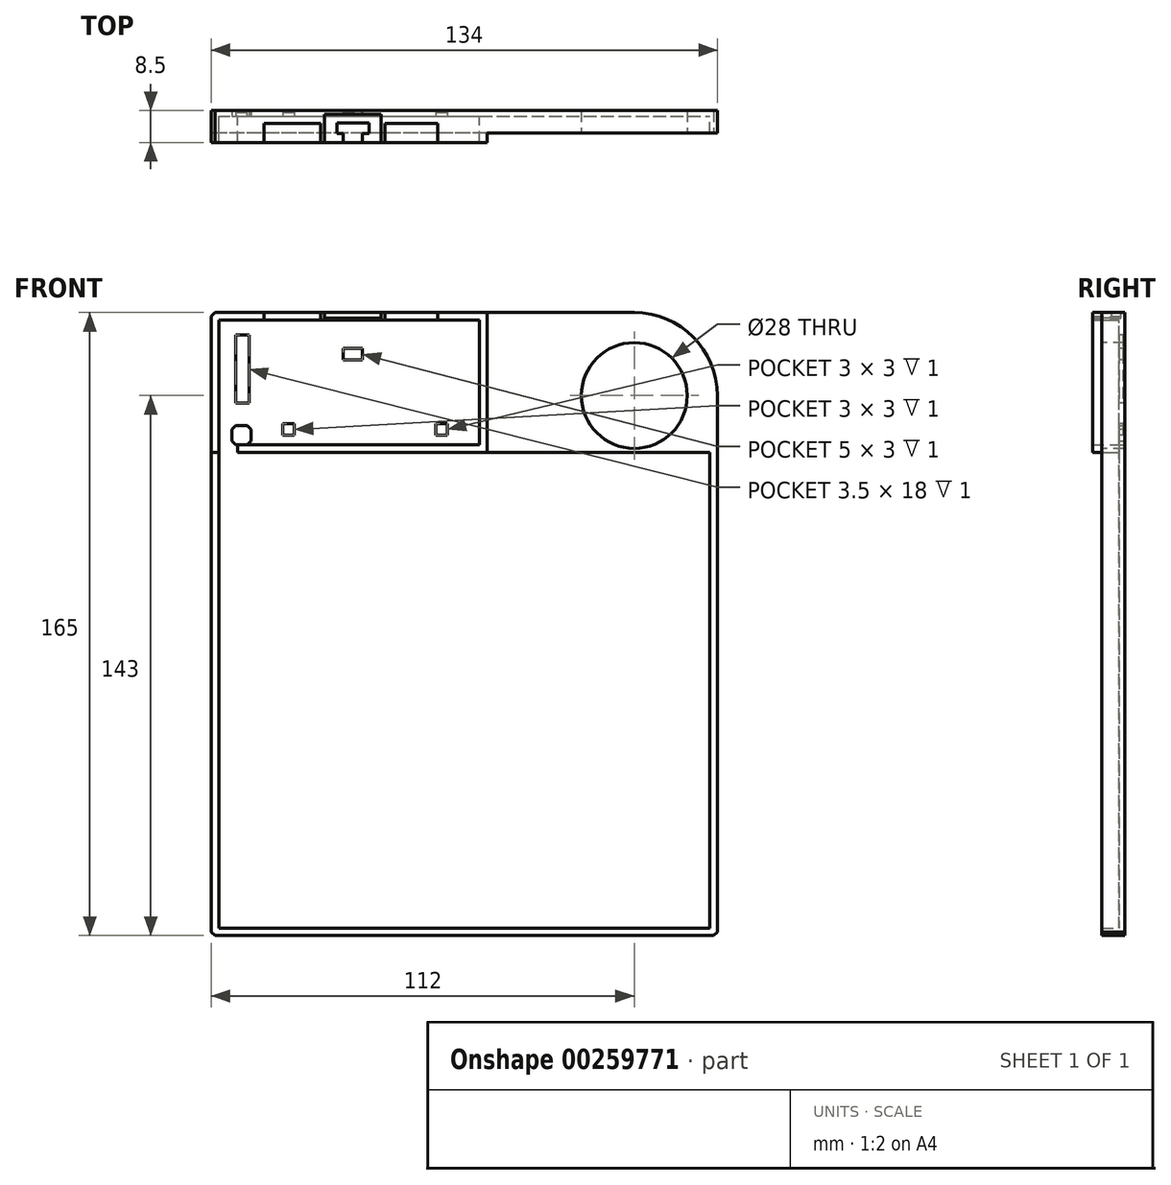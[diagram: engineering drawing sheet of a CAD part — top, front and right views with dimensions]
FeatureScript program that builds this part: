
annotation { "Feature Type Name" : "Feature", "Feature Type Description" : "" }
export const myFeature = defineFeature(function(context is Context, id is Id, definition is map)
    precondition{}
    {
        {
            var Q0;
            Q0=qCreatedBy(makeId("Front.planeOp"),FACE);
            var sketch = newSketch(context, id + "F0", { "sketchPlane" : qUnion([Q0])});
            skLineSegment(sketch, "E0.bottom", {"start": v(65, -63) * mm, "end": v(-65, -63) * mm});
            skLineSegment(sketch, "E0.top", {"start": v(65, 63) * mm, "end": v(-60, 63) * mm});
            skLineSegment(sketch, "E0.left", {"start": v(65, -63) * mm, "end": v(65, 63) * mm});
            skLineSegment(sketch, "E0.right", {"start": v(-65, -63) * mm, "end": v(-65, 63) * mm});
            skPoint(sketch, "E0.middle", {"position": v(0, 0) * mm});
            skLineSegment(sketch, "E1.0", {"start": v(67, -65) * mm, "end": v(-67, -65) * mm});
            skLineSegment(sketch, "E1.1", {"start": v(67, -65) * mm, "end": v(67, 65) * mm});
            skLineSegment(sketch, "E1.2", {"start": v(4, 65) * mm, "end": v(-60, 65) * mm});
            skLineSegment(sketch, "E1.3", {"start": v(-67, -65) * mm, "end": v(-67, 100) * mm});
            skLineSegment(sketch, "E2", {"start": v(-65, 63) * mm, "end": v(-65, 68) * mm});
            skLineSegment(sketch, "E3", {"start": v(-60, 63) * mm, "end": v(-60, 65) * mm});
            skLineSegment(sketch, "E4.top", {"start": v(-65, 98) * mm, "end": v(-53, 98) * mm});
            skLineSegment(sketch, "E4.left", {"start": v(-65, 68) * mm, "end": v(-65, 98) * mm});
            skLineSegment(sketch, "E4.right", {"start": v(4, 65) * mm, "end": v(4, 98) * mm});
            skLineSegment(sketch, "E5", {"start": v(-67, 100) * mm, "end": v(-53, 100) * mm});
            skLineSegment(sketch, "E6", {"start": v(67, 100) * mm, "end": v(67, 65) * mm});
            skLineSegment(sketch, "E7", {"start": v(-53, 100) * mm, "end": v(-53, 98) * mm});
            skLineSegment(sketch, "E8", {"start": v(-38, 100) * mm, "end": v(-38, 98) * mm});
            skLineSegment(sketch, "E9", {"start": v(-21, 100) * mm, "end": v(-21, 98) * mm});
            skLineSegment(sketch, "E10", {"start": v(-7, 100) * mm, "end": v(-7, 98) * mm});
            skLineSegment(sketch, "E11.trimOffspring", {"start": v(-38, 98) * mm, "end": v(-21, 98) * mm});
            skLineSegment(sketch, "E12.trimOffspring", {"start": v(-38, 100) * mm, "end": v(-21, 100) * mm});
            skLineSegment(sketch, "E13.trimOffspring", {"start": v(-7, 100) * mm, "end": v(67, 100) * mm});
            skLineSegment(sketch, "E14.trimOffspring", {"start": v(-7, 98) * mm, "end": v(4, 98) * mm});
            skSolve(sketch);
        }
        {
            var Q0;
            Q0 = qSketchRegion(id + "F0", true);
            extrude(context, id + "F1", {"entities" : qUnion([Q0]), "depth" : 5 * mm});
        }
        {
            var Q0;
            Q0=makeQuery(id+"F1.opExtrude","SWEPT_EDGE",EDGE,{"disambiguationData":[OSD([sQuery(id+"F0.wireOp",EDGE,"E1.3"),sQuery(id+"F0.wireOp",EDGE,"E5")])]});
            var Q1;
            Q1=makeQuery(id+"F1.opExtrude","SWEPT_EDGE",EDGE,{"disambiguationData":[OSD([sQuery(id+"F0.wireOp",EDGE,"E1.0"),sQuery(id+"F0.wireOp",EDGE,"E1.3")])]});
            var Q2;
            Q2=makeQuery(id+"F1.opExtrude","SWEPT_EDGE",EDGE,{"disambiguationData":[OSD([sQuery(id+"F0.wireOp",EDGE,"E1.0"),sQuery(id+"F0.wireOp",EDGE,"E1.1")])]});
            chamfer(context, id + "F2", {"entities" : qUnion([Q0, Q1, Q2]), "width" : 1 * mm, "tangentPropagation" : true});
        }
        {
            var Q0;
            Q0=makeQuery(id+"F1.opExtrude","CAP_FACE",FACE,{"disambiguationData":[OSD([sQuery(id+"F0.wireOp",EDGE,"E0.bottom"),sQuery(id+"F0.wireOp",EDGE,"E0.top"),sQuery(id+"F0.wireOp",EDGE,"E0.left"),sQuery(id+"F0.wireOp",EDGE,"E0.right"),sQuery(id+"F0.wireOp",EDGE,"E1.0"),sQuery(id+"F0.wireOp",EDGE,"E1.1"),sQuery(id+"F0.wireOp",EDGE,"E1.2"),sQuery(id+"F0.wireOp",EDGE,"E1.3"),sQuery(id+"F0.wireOp",EDGE,"E2"),sQuery(id+"F0.wireOp",EDGE,"E3"),sQuery(id+"F0.wireOp",EDGE,"E4.top"),sQuery(id+"F0.wireOp",EDGE,"E4.left"),sQuery(id+"F0.wireOp",EDGE,"E4.right"),sQuery(id+"F0.wireOp",EDGE,"E5"),sQuery(id+"F0.wireOp",EDGE,"E6"),sQuery(id+"F0.wireOp",EDGE,"E7"),sQuery(id+"F0.wireOp",EDGE,"E10"),sQuery(id+"F0.wireOp",EDGE,"E13.trimOffspring"),sQuery(id+"F0.wireOp",EDGE,"E14.trimOffspring")])],"isStart":true});
            var sketch = newSketch(context, id + "F3", { "sketchPlane" : qUnion([Q0])});
            skLineSegment(sketch, "E15", {"start": v(-67, -64) * mm, "end": v(-66, -65) * mm});
            skLineSegment(sketch, "E16", {"start": v(-66, -65) * mm, "end": v(66, -65) * mm});
            skLineSegment(sketch, "E17", {"start": v(66, -65) * mm, "end": v(67, -64) * mm});
            skLineSegment(sketch, "E18", {"start": v(67, -64) * mm, "end": v(67, 99) * mm});
            skLineSegment(sketch, "E19", {"start": v(67, 99) * mm, "end": v(66, 100) * mm});
            skLineSegment(sketch, "E20", {"start": v(66, 100) * mm, "end": v(53, 100) * mm});
            skLineSegment(sketch, "E21", {"start": v(53, 98) * mm, "end": v(53, 98) * mm});
            skLineSegment(sketch, "E22", {"start": v(53, 100) * mm, "end": v(53, 98) * mm, "construction": true});
            skLineSegment(sketch, "E23", {"start": v(-65, -63) * mm, "end": v(65, -63) * mm, "construction": true});
            skLineSegment(sketch, "E24", {"start": v(-65, -63) * mm, "end": v(-65, 63) * mm, "construction": true});
            skLineSegment(sketch, "E25", {"start": v(-4, 65) * mm, "end": v(60, 65) * mm, "construction": true});
            skLineSegment(sketch, "E26", {"start": v(7, 98) * mm, "end": v(-4, 98) * mm, "construction": true});
            skLineSegment(sketch, "E27", {"start": v(7, 100) * mm, "end": v(7, 98) * mm, "construction": true});
            skLineSegment(sketch, "E28", {"start": v(7, 100) * mm, "end": v(-67, 100) * mm});
            skLineSegment(sketch, "E29", {"start": v(-67, 100) * mm, "end": v(-67, -64) * mm});
            skLineSegment(sketch, "E30", {"start": v(38, 98) * mm, "end": v(21, 98) * mm, "construction": true});
            skLineSegment(sketch, "E31", {"start": v(38, 100) * mm, "end": v(38, 98) * mm, "construction": true});
            skLineSegment(sketch, "E32", {"start": v(38, 100) * mm, "end": v(21, 100) * mm});
            skLineSegment(sketch, "E33", {"start": v(21, 100) * mm, "end": v(21, 98) * mm, "construction": true});
            skLineSegment(sketch, "E34", {"start": v(53, 100) * mm, "end": v(38, 100) * mm});
            skLineSegment(sketch, "E35", {"start": v(21, 100) * mm, "end": v(7, 100) * mm});
            skLineSegment(sketch, "E36.0", {"start": v(-4, 65) * mm, "end": v(-4, 98) * mm, "construction": true});
            skLineSegment(sketch, "E37.0", {"start": v(65, 98) * mm, "end": v(53, 98) * mm, "construction": true});
            skLineSegment(sketch, "E37.1", {"start": v(65, -63) * mm, "end": v(65, 98) * mm, "construction": true});
            skLineSegment(sketch, "E38.0", {"start": v(60, 63) * mm, "end": v(60, 65) * mm, "construction": true});
            skLineSegment(sketch, "E38.1", {"start": v(-65, 63) * mm, "end": v(60, 63) * mm, "construction": true});
            skSolve(sketch);
        }
        {
            var Q0;
            Q0 = qSketchRegion(id + "F3", true);
            var Q1;
            Q1=makeQuery(id+"F3.imprint","IMPRINT",FACE,{"disambiguationData":[TD([[makeQuery(id+"F3.imprint","IMPRINT",EDGE,{"derivedFrom":sQuery(id+"F3.wireOp",EDGE,"E15")}),1.0]])]});
            var Q2;
            Q2=makeQuery(id+"F3.imprint","IMPRINT",FACE,{"disambiguationData":[TD([[makeQuery(id+"F3.imprint","IMPRINT",EDGE,{"derivedFrom":sQuery(id+"F3.wireOp",EDGE,"E32")}),1.0]])]});
            extrude(context, id + "F4", {"entities" : qUnion([Q0, Q1, Q2]), "operationType" : NewBodyOperationType.ADD, "depth" : 3.5 * mm});
        }
        {
            var Q0;
            Q0=makeQuery(id+"F4.opExtrude","CAP_FACE",FACE,{"disambiguationData":[OSD([sQuery(id+"F3.wireOp",EDGE,"E15"),sQuery(id+"F3.wireOp",EDGE,"E16"),sQuery(id+"F3.wireOp",EDGE,"E17"),sQuery(id+"F3.wireOp",EDGE,"E18"),sQuery(id+"F3.wireOp",EDGE,"E19"),sQuery(id+"F3.wireOp",EDGE,"E20"),sQuery(id+"F3.wireOp",EDGE,"E28"),sQuery(id+"F3.wireOp",EDGE,"E168"),sQuery(id+"F3.wireOp",EDGE,"E29"),sQuery(id+"F3.wireOp",EDGE,"E32"),sQuery(id+"F3.wireOp",EDGE,"E34"),sQuery(id+"F3.wireOp",EDGE,"E35")])],"isStart":true});
            var sketch = newSketch(context, id + "F5", { "sketchPlane" : qUnion([Q0])});
            skLineSegment(sketch, "E39.bottom", {"start": v(-65, 98) * mm, "end": v(4, 98) * mm});
            skLineSegment(sketch, "E39.top", {"start": v(-65, 65) * mm, "end": v(4, 65) * mm});
            skLineSegment(sketch, "E39.left", {"start": v(-65, 98) * mm, "end": v(-65, 65) * mm});
            skLineSegment(sketch, "E39.right", {"start": v(4, 98) * mm, "end": v(4, 65) * mm});
            skSolve(sketch);
        }
        {
            var Q0;
            Q0 = qSketchRegion(id + "F5", true);
            extrude(context, id + "F6", {"entities" : qUnion([Q0]), "operationType" : NewBodyOperationType.REMOVE, "oppositeDirection" : true, "depth" : 2 * mm});
        }
        {
            var Q0;
            Q0=makeQuery(id+"F6.boolean.opBoolean","COPY",FACE,{"derivedFrom":makeQuery(id+"F6.opExtrude","CAP_FACE",FACE,{"disambiguationData":[OSD([sQuery(id+"F5.wireOp",EDGE,"E39.bottom"),sQuery(id+"F5.wireOp",EDGE,"E39.top"),sQuery(id+"F5.wireOp",EDGE,"E39.left"),sQuery(id+"F5.wireOp",EDGE,"E39.right")])],"isStart":false})});
            var sketch = newSketch(context, id + "F7", { "sketchPlane" : qUnion([Q0])});
            skLineSegment(sketch, "E40.bottom", {"start": v(-61.5, 70) * mm, "end": v(-56.5, 70) * mm});
            skLineSegment(sketch, "E40.top", {"start": v(-61.5, 65) * mm, "end": v(-56.5, 65) * mm});
            skLineSegment(sketch, "E40.left", {"start": v(-61.5, 70) * mm, "end": v(-61.5, 65) * mm});
            skLineSegment(sketch, "E40.right", {"start": v(-56.5, 70) * mm, "end": v(-56.5, 65) * mm});
            skSolve(sketch);
        }
        {
            var Q0;
            Q0 = qSketchRegion(id + "F7", true);
            extrude(context, id + "F8", {"entities" : qUnion([Q0]), "operationType" : NewBodyOperationType.REMOVE, "endBound" : BoundingType.THROUGH_ALL, "oppositeDirection" : true, "depth" : 25 * mm});
        }
        {
            var Q0;
            Q0=makeQuery(id+"F8.boolean.opBoolean","COPY",EDGE,{"derivedFrom":makeQuery(id+"F8.opExtrude","SWEPT_EDGE",EDGE,{"disambiguationData":[OSD([sQuery(id+"F5.wireOp",EDGE,"E39.top"),sQuery(id+"F7.wireOp",EDGE,"E40.top"),sQuery(id+"F7.wireOp",EDGE,"E40.left")])]})});
            var Q1;
            Q1=makeQuery(id+"F8.boolean.opBoolean","COPY",EDGE,{"derivedFrom":makeQuery(id+"F8.opExtrude","SWEPT_EDGE",EDGE,{"disambiguationData":[OSD([sQuery(id+"F5.wireOp",EDGE,"E39.top"),sQuery(id+"F7.wireOp",EDGE,"E40.top"),sQuery(id+"F7.wireOp",EDGE,"E40.right")])]})});
            var Q2;
            Q2=makeQuery(id+"F8.boolean.opBoolean","COPY",EDGE,{"derivedFrom":makeQuery(id+"F8.opExtrude","SWEPT_EDGE",EDGE,{"disambiguationData":[OSD([sQuery(id+"F7.wireOp",EDGE,"E40.bottom"),sQuery(id+"F7.wireOp",EDGE,"E40.right")])]})});
            var Q3;
            Q3=makeQuery(id+"F8.boolean.opBoolean","COPY",EDGE,{"derivedFrom":makeQuery(id+"F8.opExtrude","SWEPT_EDGE",EDGE,{"disambiguationData":[OSD([sQuery(id+"F7.wireOp",EDGE,"E40.bottom"),sQuery(id+"F7.wireOp",EDGE,"E40.left")])]})});
            chamfer(context, id + "F9", {"entities" : qUnion([Q0, Q1, Q2, Q3]), "width" : 1 * mm, "tangentPropagation" : true});
        }
        {
            var Q0;
            Q0=makeQuery(id+"F6.boolean.opBoolean","COPY",FACE,{"derivedFrom":makeQuery(id+"F6.opExtrude","CAP_FACE",FACE,{"disambiguationData":[OSD([sQuery(id+"F5.wireOp",EDGE,"E39.bottom"),sQuery(id+"F5.wireOp",EDGE,"E39.top"),sQuery(id+"F5.wireOp",EDGE,"E39.left"),sQuery(id+"F5.wireOp",EDGE,"E39.right")])],"isStart":false})});
            var sketch = newSketch(context, id + "F10", { "sketchPlane" : qUnion([Q0])});
            skLineSegment(sketch, "E41.bottom", {"start": v(-60.5, 94) * mm, "end": v(-57, 94) * mm});
            skLineSegment(sketch, "E41.top", {"start": v(-60.5, 76) * mm, "end": v(-57, 76) * mm});
            skLineSegment(sketch, "E41.left", {"start": v(-60.5, 94) * mm, "end": v(-60.5, 76) * mm});
            skLineSegment(sketch, "E41.right", {"start": v(-57, 94) * mm, "end": v(-57, 76) * mm});
            skLineSegment(sketch, "E42.bottom", {"start": v(-32, 90.5) * mm, "end": v(-27, 90.5) * mm});
            skLineSegment(sketch, "E42.top", {"start": v(-32, 87.5) * mm, "end": v(-27, 87.5) * mm});
            skLineSegment(sketch, "E42.left", {"start": v(-32, 90.5) * mm, "end": v(-32, 87.5) * mm});
            skLineSegment(sketch, "E42.right", {"start": v(-27, 90.5) * mm, "end": v(-27, 87.5) * mm});
            skLineSegment(sketch, "E43.bottom", {"start": v(-48, 70.5) * mm, "end": v(-45, 70.5) * mm});
            skLineSegment(sketch, "E43.top", {"start": v(-48, 67.5) * mm, "end": v(-45, 67.5) * mm});
            skLineSegment(sketch, "E43.left", {"start": v(-48, 70.5) * mm, "end": v(-48, 67.5) * mm});
            skLineSegment(sketch, "E43.right", {"start": v(-45, 70.5) * mm, "end": v(-45, 67.5) * mm});
            skLineSegment(sketch, "E44.bottom", {"start": v(-7.5, 70.5) * mm, "end": v(-4.5, 70.5) * mm});
            skLineSegment(sketch, "E44.top", {"start": v(-7.5, 67.5) * mm, "end": v(-4.5, 67.5) * mm});
            skLineSegment(sketch, "E44.left", {"start": v(-7.5, 70.5) * mm, "end": v(-7.5, 67.5) * mm});
            skLineSegment(sketch, "E44.right", {"start": v(-4.5, 70.5) * mm, "end": v(-4.5, 67.5) * mm});
            skSolve(sketch);
        }
        {
            var Q0;
            Q0 = qSketchRegion(id + "F10", true);
            extrude(context, id + "F11", {"entities" : qUnion([Q0]), "operationType" : NewBodyOperationType.REMOVE, "oppositeDirection" : true, "depth" : 1 * mm});
        }
        {
            var Q0;
            Q0=makeQuery(id+"F1.opExtrude","SWEPT_FACE",FACE,{"disambiguationData":[OSD([sQuery(id+"F0.wireOp",EDGE,"E12.trimOffspring")])]});
            var sketch = newSketch(context, id + "F12", { "sketchPlane" : qUnion([Q0])});
            skLineSegment(sketch, "E45.bottom", {"start": v(-22, -5) * mm, "end": v(-37, -5) * mm});
            skLineSegment(sketch, "E45.top", {"start": v(-22, 2.5) * mm, "end": v(-37, 2.5) * mm});
            skLineSegment(sketch, "E45.left", {"start": v(-22, -5) * mm, "end": v(-22, 2.5) * mm});
            skLineSegment(sketch, "E45.right", {"start": v(-37, -5) * mm, "end": v(-37, 2.5) * mm});
            skSolve(sketch);
        }
        {
            var Q0;
            Q0 = qSketchRegion(id + "F12", true);
            extrude(context, id + "F13", {"entities" : qUnion([Q0]), "operationType" : NewBodyOperationType.REMOVE, "oppositeDirection" : true, "depth" : 1.5 * mm});
        }
        {
            var Q0;
            Q0=makeQuery(id+"F1.opExtrude","SWEPT_FACE",FACE,{"disambiguationData":[OSD([sQuery(id+"F0.wireOp",EDGE,"E11.trimOffspring")])]});
            var sketch = newSketch(context, id + "F14", { "sketchPlane" : qUnion([Q0])});
            skLineSegment(sketch, "E46.bottom", {"start": v(-33.75, 2.6) * mm, "end": v(-32, 2.6) * mm});
            skLineSegment(sketch, "E46.top", {"start": v(-33.75, -0.15) * mm, "end": v(-25.25, -0.15) * mm});
            skLineSegment(sketch, "E46.left", {"start": v(-33.75, 2.6) * mm, "end": v(-33.75, -0.15) * mm});
            skLineSegment(sketch, "E46.right", {"start": v(-25.25, 2.6) * mm, "end": v(-25.25, -0.15) * mm});
            skLineSegment(sketch, "E47", {"start": v(-29.5, -0.15) * mm, "end": v(-29.5, -2.5) * mm, "construction": true});
            skArc(sketch, "E48", {"start": v(-32, 5) * mm, "mid": v(-29.5, 2.6) * mm, "end": v(-27, 5) * mm, "construction": true});
            skLineSegment(sketch, "E49", {"start": v(-29.5, 5.1) * mm, "end": v(-29.5, -0.15) * mm, "construction": true});
            skLineSegment(sketch, "E50", {"start": v(-32, 5) * mm, "end": v(-27, 5) * mm});
            skLineSegment(sketch, "E51", {"start": v(-32, 5) * mm, "end": v(-32, 2.6) * mm});
            skLineSegment(sketch, "E52", {"start": v(-27, 5) * mm, "end": v(-27, 2.6) * mm});
            skLineSegment(sketch, "E53.trimOffspring", {"start": v(-27, 2.6) * mm, "end": v(-25.25, 2.6) * mm});
            skSolve(sketch);
        }
        {
            var Q0;
            Q0=makeQuery(id+"F14.imprint","IMPRINT",FACE,{"disambiguationData":[TD([[makeQuery(id+"F14.imprint","IMPRINT",EDGE,{"derivedFrom":sQuery(id+"F14.wireOp",EDGE,"E46.top")}),1.0]])]});
            var Q1;
            {var subQ0=sQuery(id+"F14.wireOp",EDGE,"E48");var subQ1=makeQuery(id+"F14.imprint","INTERSECT",VERTEX,{"derivedFrom":[sQuery(id+"F14.wireOp",EDGE,"E46.bottom"),subQ0]});Q1=makeQuery(id+"F14.imprint","IMPRINT",FACE,{"disambiguationData":[TD([[makeQuery(id+"F14.imprint","IMPRINT",EDGE,{"disambiguationData":[TD([[subQ1,1.0]])],"derivedFrom":subQ0}),1.0]])]});}
            extrude(context, id + "F15", {"entities" : qUnion([Q0, Q1]), "operationType" : NewBodyOperationType.REMOVE, "endBound" : BoundingType.THROUGH_ALL, "oppositeDirection" : true, "depth" : 25 * mm});
        }
        {
            var Q0;
            Q0=makeQuery(id+"F1.opExtrude","SWEPT_EDGE",EDGE,{"disambiguationData":[OSD([sQuery(id+"F0.wireOp",EDGE,"E6"),sQuery(id+"F0.wireOp",EDGE,"E13.trimOffspring")])]});
            var Q1;
            Q1=makeQuery(id+"F4.opExtrude","SWEPT_EDGE",EDGE,{"disambiguationData":[OSD([sQuery(id+"F0.wireOp",EDGE,"E1.1"),sQuery(id+"F0.wireOp",EDGE,"E6"),sQuery(id+"F0.wireOp",EDGE,"E13.trimOffspring")])]});
            fillet(context, id + "F16", {"entities" : qUnion([Q0, Q1]), "radius" : 22 * mm, "tangentPropagation" : true, "allowEdgeOverflow" : false});
        }
        {
            var Q0;
            Q0=makeQuery(id+"F1.opExtrude","CAP_FACE",FACE,{"disambiguationData":[OSD([sQuery(id+"F0.wireOp",EDGE,"E0.bottom"),sQuery(id+"F0.wireOp",EDGE,"E0.top"),sQuery(id+"F0.wireOp",EDGE,"E0.left"),sQuery(id+"F0.wireOp",EDGE,"E0.right"),sQuery(id+"F0.wireOp",EDGE,"E1.0"),sQuery(id+"F0.wireOp",EDGE,"E1.1"),sQuery(id+"F0.wireOp",EDGE,"E1.2"),sQuery(id+"F0.wireOp",EDGE,"E1.3"),sQuery(id+"F0.wireOp",EDGE,"E2"),sQuery(id+"F0.wireOp",EDGE,"E3"),sQuery(id+"F0.wireOp",EDGE,"E4.top"),sQuery(id+"F0.wireOp",EDGE,"E4.left"),sQuery(id+"F0.wireOp",EDGE,"E4.right"),sQuery(id+"F0.wireOp",EDGE,"E5"),sQuery(id+"F0.wireOp",EDGE,"E6"),sQuery(id+"F0.wireOp",EDGE,"E7"),sQuery(id+"F0.wireOp",EDGE,"E10"),sQuery(id+"F0.wireOp",EDGE,"E13.trimOffspring"),sQuery(id+"F0.wireOp",EDGE,"E14.trimOffspring")])],"isStart":false});
            var sketch = newSketch(context, id + "F17", { "sketchPlane" : qUnion([Q0])});
            skSolve(sketch);
        }
        {
            var Q0;
            {var subQ18=sQuery(id+"F0.wireOp",EDGE,"E0.bottom");Q0=makeQuery(id+"F17.imprint","IMPRINT",FACE,{"disambiguationData":[TD([[makeQuery(id+"F17.imprint","IMPRINT",EDGE,{"derivedFrom":makeQuery(id+"F1.opExtrude","CAP_EDGE",EDGE,{"disambiguationData":[OSD([subQ18])],"isStart":false})}),1.0]])]});}
            var sketch = newSketch(context, id + "F18", { "sketchPlane" : qUnion([Q0])});
            skCircle(sketch, "E54", {"center": v(45, 78) * mm, "radius": 14 * mm});
            skSolve(sketch);
        }
        {
            var Q0;
            Q0 = qSketchRegion(id + "F18", true);
            extrude(context, id + "F19", {"entities" : qUnion([Q0]), "operationType" : NewBodyOperationType.REMOVE, "endBound" : BoundingType.THROUGH_ALL, "oppositeDirection" : true, "depth" : 25 * mm});
        }
        {
            var Q0;
            Q0=makeQuery(id+"F6.boolean.opBoolean","SPLIT",FACE,{"disambiguationData":[TD([makeQuery(id+"F1.opExtrude","SWEPT_FACE",FACE,{"disambiguationData":[OSD([sQuery(id+"F0.wireOp",EDGE,"E0.bottom")])]})])],"derivedFrom":makeQuery(id+"F4.opExtrude","CAP_FACE",FACE,{"disambiguationData":[OSD([sQuery(id+"F3.wireOp",EDGE,"E15"),sQuery(id+"F3.wireOp",EDGE,"E16"),sQuery(id+"F3.wireOp",EDGE,"E17"),sQuery(id+"F3.wireOp",EDGE,"E18"),sQuery(id+"F3.wireOp",EDGE,"E19"),sQuery(id+"F3.wireOp",EDGE,"E20"),sQuery(id+"F3.wireOp",EDGE,"E29"),sQuery(id+"F3.wireOp",EDGE,"E32"),sQuery(id+"F3.wireOp",EDGE,"E34"),sQuery(id+"F3.wireOp",EDGE,"E35"),sQuery(id+"F3.wireOp",EDGE,"E28")])],"isStart":true})});
            var sketch = newSketch(context, id + "F20", { "sketchPlane" : qUnion([Q0])});
            skLineSegment(sketch, "E55.0", {"start": v(-65, 65) * mm, "end": v(-60, 65) * mm});
            skLineSegment(sketch, "E55.1", {"start": v(65, 63) * mm, "end": v(-60, 63) * mm});
            skLineSegment(sketch, "E55.2", {"start": v(-60, 63) * mm, "end": v(-60, 65) * mm});
            skLineSegment(sketch, "E55.3", {"start": v(65, -63) * mm, "end": v(65, 63) * mm});
            skLineSegment(sketch, "E55.4", {"start": v(65, -63) * mm, "end": v(-65, -63) * mm});
            skLineSegment(sketch, "E55.5", {"start": v(-65, -63) * mm, "end": v(-65, 65) * mm});
            skPoint(sketch, "E55.6", {"position": v(-60, 64) * mm});
            skSolve(sketch);
        }
        {
            var Q0;
            Q0 = qSketchRegion(id + "F20", true);
            var Q1;
            Q1=makeQuery(id+"F6.boolean.opBoolean","COPY",FACE,{"derivedFrom":makeQuery(id+"F6.opExtrude","CAP_FACE",FACE,{"disambiguationData":[OSD([sQuery(id+"F5.wireOp",EDGE,"E39.bottom"),sQuery(id+"F5.wireOp",EDGE,"E39.top"),sQuery(id+"F5.wireOp",EDGE,"E39.left"),sQuery(id+"F5.wireOp",EDGE,"E39.right")])],"isStart":false})});
            extrude(context, id + "F21", {"entities" : qUnion([Q0]), "operationType" : NewBodyOperationType.REMOVE, "endBound" : BoundingType.UP_TO_SURFACE, "oppositeDirection" : true, "endBoundEntityFace" : qUnion([Q1]), "depth" : 25 * mm});
        }
        {
            var Q0;
            {var subQ18=sQuery(id+"F0.wireOp",EDGE,"E0.bottom");Q0=makeQuery(id+"F17.imprint","IMPRINT",FACE,{"disambiguationData":[TD([[makeQuery(id+"F17.imprint","IMPRINT",EDGE,{"derivedFrom":makeQuery(id+"F1.opExtrude","CAP_EDGE",EDGE,{"disambiguationData":[OSD([subQ18])],"isStart":false})}),1.0]])]});}
            var sketch = newSketch(context, id + "F22", { "sketchPlane" : qUnion([Q0])});
            skLineSegment(sketch, "E56.0", {"start": v(6, 62.85) * mm, "end": v(6, 100.2) * mm});
            skLineSegment(sketch, "E57.0", {"start": v(6, 100) * mm, "end": v(45, 100) * mm});
            skArc(sketch, "E58.0", {"start": v(67, 78) * mm, "mid": v(60.56, 93.56) * mm, "end": v(45, 100) * mm});
            skLineSegment(sketch, "E59.0", {"start": v(67, 78) * mm, "end": v(67, -64) * mm});
            skLineSegment(sketch, "E60.0", {"start": v(6, 63) * mm, "end": v(-67, 63) * mm});
            skLineSegment(sketch, "E61.0", {"start": v(-67, -64) * mm, "end": v(-67, 63) * mm});
            skLineSegment(sketch, "E62.0", {"start": v(66, -65) * mm, "end": v(-66, -65) * mm});
            skPoint(sketch, "E63.orphan", {"position": v(-60, 63) * mm});
            skPoint(sketch, "E64.orphan", {"position": v(-7, 100) * mm});
            skPoint(sketch, "E65.orphan", {"position": v(65, 63) * mm});
            skPoint(sketch, "E66.orphan", {"position": v(-67, 99) * mm});
            skLineSegment(sketch, "E67.0", {"start": v(66, -65) * mm, "end": v(67, -64) * mm});
            skLineSegment(sketch, "E68.0", {"start": v(-67, -64) * mm, "end": v(-66, -65) * mm});
            skSolve(sketch);
        }
        {
            var Q0;
            Q0 = qSketchRegion(id + "F22", true);
            extrude(context, id + "F23", {"entities" : qUnion([Q0]), "operationType" : NewBodyOperationType.REMOVE, "oppositeDirection" : true, "depth" : 2.5 * mm});
        }
    });
